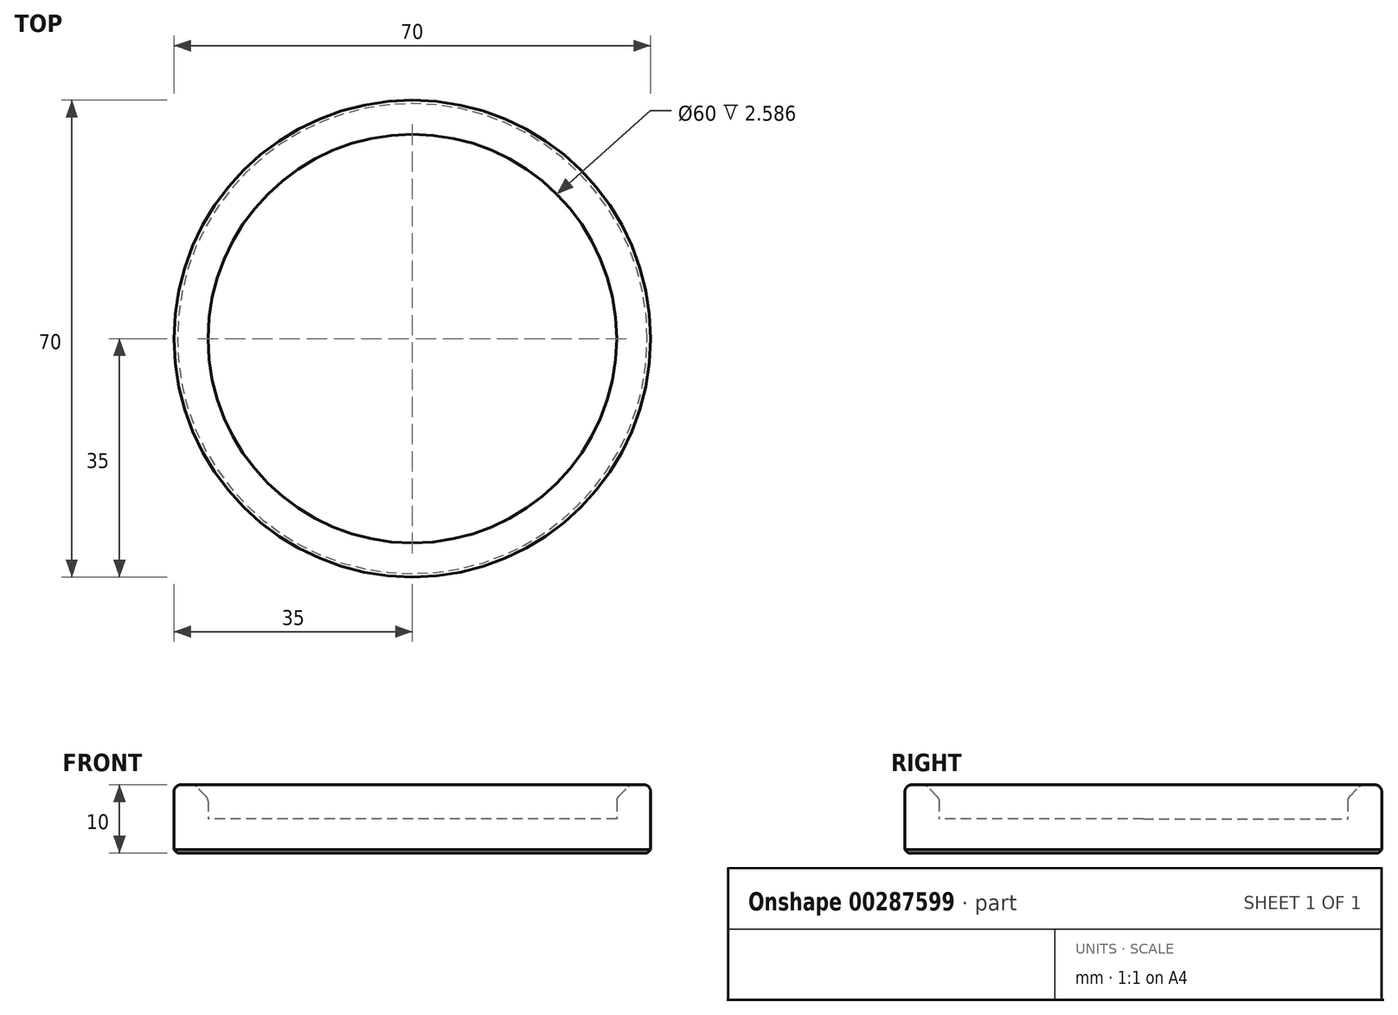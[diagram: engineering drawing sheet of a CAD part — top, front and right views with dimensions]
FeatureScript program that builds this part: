
annotation { "Feature Type Name" : "Feature", "Feature Type Description" : "" }
export const myFeature = defineFeature(function(context is Context, id is Id, definition is map)
    precondition{}
    {
        {
            var Q0;
            Q0=qCreatedBy(makeId("Top.planeOp"),FACE);
            var sketch = newSketch(context, id + "F0", { "sketchPlane" : qUnion([Q0])});
            skCircle(sketch, "E0", {"center": v(0, 0) * mm, "radius": 30 * mm});
            skCircle(sketch, "E1", {"center": v(0, 0) * mm, "radius": 35 * mm});
            skSolve(sketch);
        }
        {
            var Q0;
            Q0=makeQuery(id+"F0.imprint","IMPRINT",FACE,{"disambiguationData":[TD([[makeQuery(id+"F0.imprint","IMPRINT",EDGE,{"derivedFrom":sQuery(id+"F0.wireOp",EDGE,"E0")}),1.0]])]});
            extrude(context, id + "F1", {"entities" : qUnion([Q0]), "depth" : 5 * mm, "offsetDistance" : 25 * mm});
        }
        {
            var Q0;
            Q0=makeQuery(id+"F0.imprint","IMPRINT",FACE,{"disambiguationData":[TD([[makeQuery(id+"F0.imprint","IMPRINT",EDGE,{"derivedFrom":sQuery(id+"F0.wireOp",EDGE,"E0")}),-1.0]])]});
            extrude(context, id + "F2", {"entities" : qUnion([Q0]), "operationType" : NewBodyOperationType.ADD, "depth" : (5 + 5) * mm, "offsetDistance" : 25 * mm});
        }
        {
            var Q0;
            Q0=makeQuery(id+"F2.opExtrude","CAP_EDGE",EDGE,{"disambiguationData":[OSD([sQuery(id+"F0.wireOp",EDGE,"E0")])],"isStart":false});
            chamfer(context, id + "F3", {"entities" : qUnion([Q0]), "width" : 2 * mm, "tangentPropagation" : true});
        }
        {
            var Q0;
            {var subQ0=sQuery(id+"F0.wireOp",EDGE,"E0");Q0=makeQuery(id+"F3.opChamfer","BLEND_EDGE",EDGE,{"blendedFrom":[makeQuery(id+"F2.opExtrude","CAP_EDGE",EDGE,{"disambiguationData":[OSD([subQ0])],"isStart":false}),makeQuery(id+"F2.opExtrude","SWEPT_FACE",FACE,{"disambiguationData":[OSD([subQ0])]})],"blendedInto":[makeQuery(id+"F2.opExtrude","SWEPT_FACE",FACE,{"disambiguationData":[OSD([subQ0])]})]});}
            var Q1;
            {var subQ0=sQuery(id+"F0.wireOp",EDGE,"E0");Q1=makeQuery(id+"F3.opChamfer","BLEND_EDGE",EDGE,{"blendedFrom":[makeQuery(id+"F2.opExtrude","CAP_EDGE",EDGE,{"disambiguationData":[OSD([subQ0])],"isStart":false}),makeQuery(id+"F2.opExtrude","CAP_FACE",FACE,{"disambiguationData":[OSD([subQ0,sQuery(id+"F0.wireOp",EDGE,"E1")])],"isStart":false})],"blendedInto":[makeQuery(id+"F2.opExtrude","CAP_FACE",FACE,{"disambiguationData":[OSD([subQ0,sQuery(id+"F0.wireOp",EDGE,"E1")])],"isStart":false})]});}
            var Q2;
            Q2=makeQuery(id+"F2.opExtrude","CAP_EDGE",EDGE,{"disambiguationData":[OSD([sQuery(id+"F0.wireOp",EDGE,"E1")])],"isStart":false});
            fillet(context, id + "F4", {"entities" : qUnion([Q0, Q1, Q2]), "radius" : 1 * mm, "tangentPropagation" : true, "allowEdgeOverflow" : false});
        }
        {
            var Q0;
            Q0=makeQuery(id+"F2.opExtrude","CAP_EDGE",EDGE,{"disambiguationData":[OSD([sQuery(id+"F0.wireOp",EDGE,"E1")])],"isStart":true});
            chamfer(context, id + "F5", {"entities" : qUnion([Q0]), "width" : 0.5 * mm, "tangentPropagation" : true});
        }
    });
